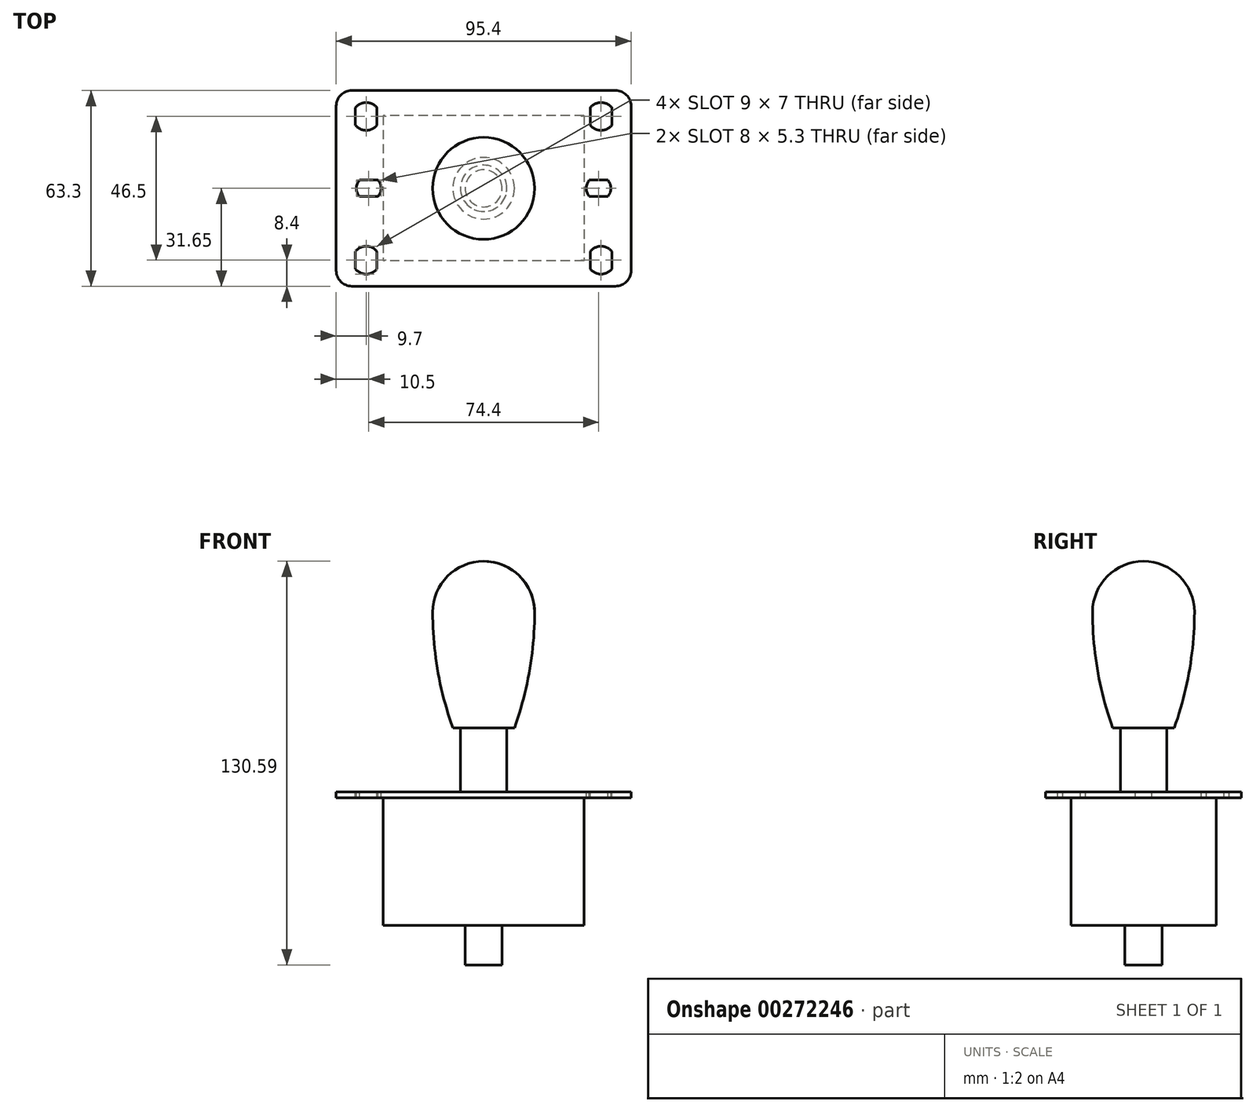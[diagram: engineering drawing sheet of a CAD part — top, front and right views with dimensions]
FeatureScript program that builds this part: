
annotation { "Feature Type Name" : "Feature", "Feature Type Description" : "" }
export const myFeature = defineFeature(function(context is Context, id is Id, definition is map)
    precondition{}
    {
        {
            var Q0;
            Q0=qCreatedBy(makeId("Top.planeOp"),FACE);
            var sketch = newSketch(context, id + "F0", { "sketchPlane" : qUnion([Q0])});
            skLineSegment(sketch, "E0.bottom", {"start": v(42.7, -31.65) * mm, "end": v(-42.7, -31.65) * mm});
            skLineSegment(sketch, "E0.top", {"start": v(42.7, 31.65) * mm, "end": v(-42.7, 31.65) * mm});
            skLineSegment(sketch, "E0.left", {"start": v(47.7, -26.65) * mm, "end": v(47.7, 26.65) * mm});
            skLineSegment(sketch, "E0.right", {"start": v(-47.7, -26.65) * mm, "end": v(-47.7, 26.65) * mm});
            skPoint(sketch, "E0.middle", {"position": v(0, 0) * mm});
            skPoint(sketch, "E1.visualSharp", {"position": v(-47.7, 31.65) * mm});
            skArc(sketch, "E1.filletArc", {"start": v(-42.7, 31.65) * mm, "mid": v(-46.24, 30.19) * mm, "end": v(-47.7, 26.65) * mm});
            skPoint(sketch, "E2.visualSharp", {"position": v(47.7, 31.65) * mm});
            skArc(sketch, "E2.filletArc", {"start": v(47.7, 26.65) * mm, "mid": v(46.24, 30.19) * mm, "end": v(42.7, 31.65) * mm});
            skPoint(sketch, "E3.visualSharp", {"position": v(47.7, -31.65) * mm});
            skArc(sketch, "E3.filletArc", {"start": v(42.7, -31.65) * mm, "mid": v(46.24, -30.19) * mm, "end": v(47.7, -26.65) * mm});
            skPoint(sketch, "E4.visualSharp", {"position": v(-47.7, -31.65) * mm});
            skArc(sketch, "E4.filletArc", {"start": v(-47.7, -26.65) * mm, "mid": v(-46.24, -30.19) * mm, "end": v(-42.7, -31.65) * mm});
            skArc(sketch, "E5", {"start": v(-34.5, 26.08) * mm, "mid": v(-38, 27.75) * mm, "end": v(-41.5, 26.08) * mm});
            skLineSegment(sketch, "E6.left", {"start": v(-34.5, 20.42) * mm, "end": v(-34.5, 26.08) * mm});
            skLineSegment(sketch, "E6.right", {"start": v(-41.5, 20.42) * mm, "end": v(-41.5, 26.08) * mm});
            skArc(sketch, "E7.trimOffspring", {"start": v(-41.5, 20.42) * mm, "mid": v(-38, 18.75) * mm, "end": v(-34.5, 20.42) * mm});
            skLineSegment(sketch, "E8.MirrorCS", {"start": v(41.5, 20.42) * mm, "end": v(41.5, 26.08) * mm});
            skLineSegment(sketch, "E9.MirrorCS", {"start": v(34.5, 20.42) * mm, "end": v(34.5, 26.08) * mm});
            skArc(sketch, "E10.MirrorCS", {"start": v(34.5, 26.08) * mm, "mid": v(38, 27.75) * mm, "end": v(41.5, 26.08) * mm});
            skArc(sketch, "E11.MirrorCS", {"start": v(41.5, 20.42) * mm, "mid": v(38, 18.75) * mm, "end": v(34.5, 20.42) * mm});
            skArc(sketch, "E12.MirrorCS", {"start": v(-41.5, -20.42) * mm, "mid": v(-38, -18.75) * mm, "end": v(-34.5, -20.42) * mm});
            skLineSegment(sketch, "E13.MirrorCS", {"start": v(-34.5, -20.42) * mm, "end": v(-34.5, -26.08) * mm});
            skLineSegment(sketch, "E14.MirrorCS", {"start": v(-41.5, -20.42) * mm, "end": v(-41.5, -26.08) * mm});
            skArc(sketch, "E15.MirrorCS", {"start": v(-34.5, -26.08) * mm, "mid": v(-38, -27.75) * mm, "end": v(-41.5, -26.08) * mm});
            skPoint(sketch, "E16.MirrorP", {"position": v(38, -23.25) * mm});
            skArc(sketch, "E17.MirrorCS", {"start": v(41.5, -20.42) * mm, "mid": v(38, -18.75) * mm, "end": v(34.5, -20.42) * mm});
            skLineSegment(sketch, "E18.MirrorCS", {"start": v(41.5, -20.42) * mm, "end": v(41.5, -26.08) * mm});
            skLineSegment(sketch, "E19.MirrorCS", {"start": v(34.5, -20.42) * mm, "end": v(34.5, -26.08) * mm});
            skArc(sketch, "E20.MirrorCS", {"start": v(34.5, -26.08) * mm, "mid": v(38, -27.75) * mm, "end": v(41.5, -26.08) * mm});
            skLineSegment(sketch, "E21", {"start": v(-38, 23.25) * mm, "end": v(38, 23.25) * mm, "construction": true});
            skLineSegment(sketch, "E22", {"start": v(-38, 23.25) * mm, "end": v(-38, -23.25) * mm, "construction": true});
            skArc(sketch, "E23", {"start": v(-34.2, -2.65) * mm, "mid": v(-33.2, 0) * mm, "end": v(-34.2, 2.65) * mm});
            skLineSegment(sketch, "E24.bottom", {"start": v(-34.2, -2.65) * mm, "end": v(-40.2, -2.65) * mm});
            skLineSegment(sketch, "E24.top", {"start": v(-34.2, 2.65) * mm, "end": v(-40.2, 2.65) * mm});
            skArc(sketch, "E25.trimOffspring", {"start": v(-40.2, 2.65) * mm, "mid": v(-41.2, 0) * mm, "end": v(-40.2, -2.65) * mm});
            skLineSegment(sketch, "E26.MirrorCS", {"start": v(34.2, 2.65) * mm, "end": v(40.2, 2.65) * mm});
            skLineSegment(sketch, "E27.MirrorCS", {"start": v(34.2, -2.65) * mm, "end": v(40.2, -2.65) * mm});
            skArc(sketch, "E28.MirrorCS", {"start": v(34.2, -2.65) * mm, "mid": v(33.2, 0) * mm, "end": v(34.2, 2.65) * mm});
            skArc(sketch, "E29.MirrorCS", {"start": v(40.2, 2.65) * mm, "mid": v(41.2, 0) * mm, "end": v(40.2, -2.65) * mm});
            skLineSegment(sketch, "E30", {"start": v(37.2, 0) * mm, "end": v(-37.2, 0) * mm, "construction": true});
            skSolve(sketch);
        }
        {
            var Q0;
            Q0=makeQuery(id+"F0.imprint","IMPRINT",FACE,{"disambiguationData":[TD([[makeQuery(id+"F0.imprint","IMPRINT",EDGE,{"derivedFrom":sQuery(id+"F0.wireOp",EDGE,"E0.bottom")}),-1.0]])]});
            var Q1;
            Q1=qCreatedBy(makeId("Top.planeOp"),FACE);
            extrude(context, id + "F1", {"entities" : qUnion([Q0]), "oppositeDirection" : true, "endBoundEntityFace" : qUnion([Q1]), "depth" : 2 * mm});
        }
        {
            var Q0;
            Q0=makeQuery(id+"F1.opExtrude","CAP_FACE",FACE,{"disambiguationData":[OSD([sQuery(id+"F0.wireOp",EDGE,"E0.bottom"),sQuery(id+"F0.wireOp",EDGE,"E0.top"),sQuery(id+"F0.wireOp",EDGE,"E0.left"),sQuery(id+"F0.wireOp",EDGE,"E0.right"),sQuery(id+"F0.wireOp",EDGE,"E1.filletArc"),sQuery(id+"F0.wireOp",EDGE,"E2.filletArc"),sQuery(id+"F0.wireOp",EDGE,"E3.filletArc"),sQuery(id+"F0.wireOp",EDGE,"E4.filletArc"),sQuery(id+"F0.wireOp",EDGE,"E9.MirrorCS"),sQuery(id+"F0.wireOp",EDGE,"E11.MirrorCS"),sQuery(id+"F0.wireOp",EDGE,"E8.MirrorCS"),sQuery(id+"F0.wireOp",EDGE,"E10.MirrorCS"),sQuery(id+"F0.wireOp",EDGE,"E12.MirrorCS"),sQuery(id+"F0.wireOp",EDGE,"E13.MirrorCS"),sQuery(id+"F0.wireOp",EDGE,"E14.MirrorCS"),sQuery(id+"F0.wireOp",EDGE,"E15.MirrorCS"),sQuery(id+"F0.wireOp",EDGE,"E7.trimOffspring"),sQuery(id+"F0.wireOp",EDGE,"E6.left"),sQuery(id+"F0.wireOp",EDGE,"E5"),sQuery(id+"F0.wireOp",EDGE,"E6.right"),sQuery(id+"F0.wireOp",EDGE,"E17.MirrorCS"),sQuery(id+"F0.wireOp",EDGE,"E18.MirrorCS"),sQuery(id+"F0.wireOp",EDGE,"E19.MirrorCS"),sQuery(id+"F0.wireOp",EDGE,"E20.MirrorCS"),sQuery(id+"F0.wireOp",EDGE,"E23"),sQuery(id+"F0.wireOp",EDGE,"E24.bottom"),sQuery(id+"F0.wireOp",EDGE,"E24.top"),sQuery(id+"F0.wireOp",EDGE,"E25.trimOffspring"),sQuery(id+"F0.wireOp",EDGE,"E26.MirrorCS"),sQuery(id+"F0.wireOp",EDGE,"E27.MirrorCS"),sQuery(id+"F0.wireOp",EDGE,"E28.MirrorCS"),sQuery(id+"F0.wireOp",EDGE,"E29.MirrorCS")])],"isStart":true});
            var sketch = newSketch(context, id + "F2", { "sketchPlane" : qUnion([Q0])});
            skCircle(sketch, "E31", {"center": v(0, 0) * mm, "radius": 7.5 * mm});
            skSolve(sketch);
        }
        {
            var Q0;
            Q0 = qSketchRegion(id + "F2", true);
            extrude(context, id + "F3", {"entities" : qUnion([Q0]), "operationType" : NewBodyOperationType.ADD, "depth" : 70 * mm});
        }
        {
            var Q0;
            Q0=qCreatedBy(makeId("Front.planeOp"),FACE);
            var sketch = newSketch(context, id + "F4", { "sketchPlane" : qUnion([Q0])});
            skArc(sketch, "E32", {"start": v(-16.5, 58.1) * mm, "mid": v(-14.84, 39.11) * mm, "end": v(-9.96, 20.7) * mm});
            skArc(sketch, "E33.MirrorCS", {"start": v(16.5, 58.1) * mm, "mid": v(16.5, 58.06) * mm, "end": v(16.5, 58.04) * mm});
            skLineSegment(sketch, "E34", {"start": v(-9.96, 20.7) * mm, "end": v(0, 20.7) * mm});
            skArc(sketch, "E35", {"start": v(16.5, 58.04) * mm, "mid": v(16.5, 58.06) * mm, "end": v(16.5, 58.1) * mm});
            skPoint(sketch, "E36", {"position": v(0, 74.6) * mm});
            skPoint(sketch, "E37", {"position": v(0, 20.7) * mm});
            skLineSegment(sketch, "E38", {"start": v(0, 74.6) * mm, "end": v(0, 20.7) * mm});
            skArc(sketch, "E39.trimOffspring", {"start": v(0, 74.6) * mm, "mid": v(-11.69, 69.74) * mm, "end": v(-16.5, 58.04) * mm});
            skSolve(sketch);
        }
        {
            var Q0;
            {var subQ1=sQuery(id+"F4.wireOp",EDGE,"E34");Q0=makeQuery(id+"F4.imprint","IMPRINT",FACE,{"disambiguationData":[TD([[makeQuery(id+"F4.imprint","IMPRINT",EDGE,{"derivedFrom":subQ1}),1.0]])]});}
            var Q1;
            Q1=sQuery(id+"F4.wireOp",EDGE,"E38");
            revolve(context, id + "F5", {"operationType" : NewBodyOperationType.ADD, "entities" : qUnion([Q0]), "axis" : qUnion([Q1]), "revolveType" : RevolveType.FULL});
        }
        {
            var Q0;
            Q0=makeQuery(id+"F1.opExtrude","CAP_FACE",FACE,{"disambiguationData":[OSD([sQuery(id+"F0.wireOp",EDGE,"E0.bottom"),sQuery(id+"F0.wireOp",EDGE,"E0.top"),sQuery(id+"F0.wireOp",EDGE,"E0.left"),sQuery(id+"F0.wireOp",EDGE,"E0.right"),sQuery(id+"F0.wireOp",EDGE,"E1.filletArc"),sQuery(id+"F0.wireOp",EDGE,"E2.filletArc"),sQuery(id+"F0.wireOp",EDGE,"E3.filletArc"),sQuery(id+"F0.wireOp",EDGE,"E4.filletArc"),sQuery(id+"F0.wireOp",EDGE,"E9.MirrorCS"),sQuery(id+"F0.wireOp",EDGE,"E11.MirrorCS"),sQuery(id+"F0.wireOp",EDGE,"E8.MirrorCS"),sQuery(id+"F0.wireOp",EDGE,"E10.MirrorCS"),sQuery(id+"F0.wireOp",EDGE,"E12.MirrorCS"),sQuery(id+"F0.wireOp",EDGE,"E13.MirrorCS"),sQuery(id+"F0.wireOp",EDGE,"E14.MirrorCS"),sQuery(id+"F0.wireOp",EDGE,"E15.MirrorCS"),sQuery(id+"F0.wireOp",EDGE,"E7.trimOffspring"),sQuery(id+"F0.wireOp",EDGE,"E6.left"),sQuery(id+"F0.wireOp",EDGE,"E5"),sQuery(id+"F0.wireOp",EDGE,"E6.right"),sQuery(id+"F0.wireOp",EDGE,"E17.MirrorCS"),sQuery(id+"F0.wireOp",EDGE,"E18.MirrorCS"),sQuery(id+"F0.wireOp",EDGE,"E19.MirrorCS"),sQuery(id+"F0.wireOp",EDGE,"E20.MirrorCS"),sQuery(id+"F0.wireOp",EDGE,"E23"),sQuery(id+"F0.wireOp",EDGE,"E24.bottom"),sQuery(id+"F0.wireOp",EDGE,"E24.top"),sQuery(id+"F0.wireOp",EDGE,"E25.trimOffspring"),sQuery(id+"F0.wireOp",EDGE,"E26.MirrorCS"),sQuery(id+"F0.wireOp",EDGE,"E27.MirrorCS"),sQuery(id+"F0.wireOp",EDGE,"E28.MirrorCS"),sQuery(id+"F0.wireOp",EDGE,"E29.MirrorCS")])],"isStart":false});
            var sketch = newSketch(context, id + "F6", { "sketchPlane" : qUnion([Q0])});
            skLineSegment(sketch, "E40.bottom", {"start": v(32.5, -23.5) * mm, "end": v(-32.5, -23.5) * mm});
            skLineSegment(sketch, "E40.top", {"start": v(32.5, 23.5) * mm, "end": v(-32.5, 23.5) * mm});
            skLineSegment(sketch, "E40.left", {"start": v(32.5, -23.5) * mm, "end": v(32.5, 23.5) * mm});
            skLineSegment(sketch, "E40.right", {"start": v(-32.5, -23.5) * mm, "end": v(-32.5, 23.5) * mm});
            skPoint(sketch, "E40.middle", {"position": v(0, 0) * mm});
            skSolve(sketch);
        }
        {
            var Q0;
            Q0 = qSketchRegion(id + "F6", true);
            extrude(context, id + "F7", {"entities" : qUnion([Q0]), "operationType" : NewBodyOperationType.ADD, "depth" : 41.2 * mm});
        }
        {
            var Q0;
            Q0=makeQuery(id+"F7.opExtrude","CAP_FACE",FACE,{"disambiguationData":[OSD([sQuery(id+"F6.wireOp",EDGE,"E40.bottom"),sQuery(id+"F6.wireOp",EDGE,"E40.top"),sQuery(id+"F6.wireOp",EDGE,"E40.left"),sQuery(id+"F6.wireOp",EDGE,"E40.right")])],"isStart":false});
            var sketch = newSketch(context, id + "F8", { "sketchPlane" : qUnion([Q0])});
            skCircle(sketch, "E41", {"center": v(0, 0) * mm, "radius": 6 * mm});
            skSolve(sketch);
        }
        {
            var Q0;
            Q0 = qSketchRegion(id + "F8", true);
            extrude(context, id + "F9", {"entities" : qUnion([Q0]), "operationType" : NewBodyOperationType.ADD, "depth" : 12.8 * mm});
        }
    });
